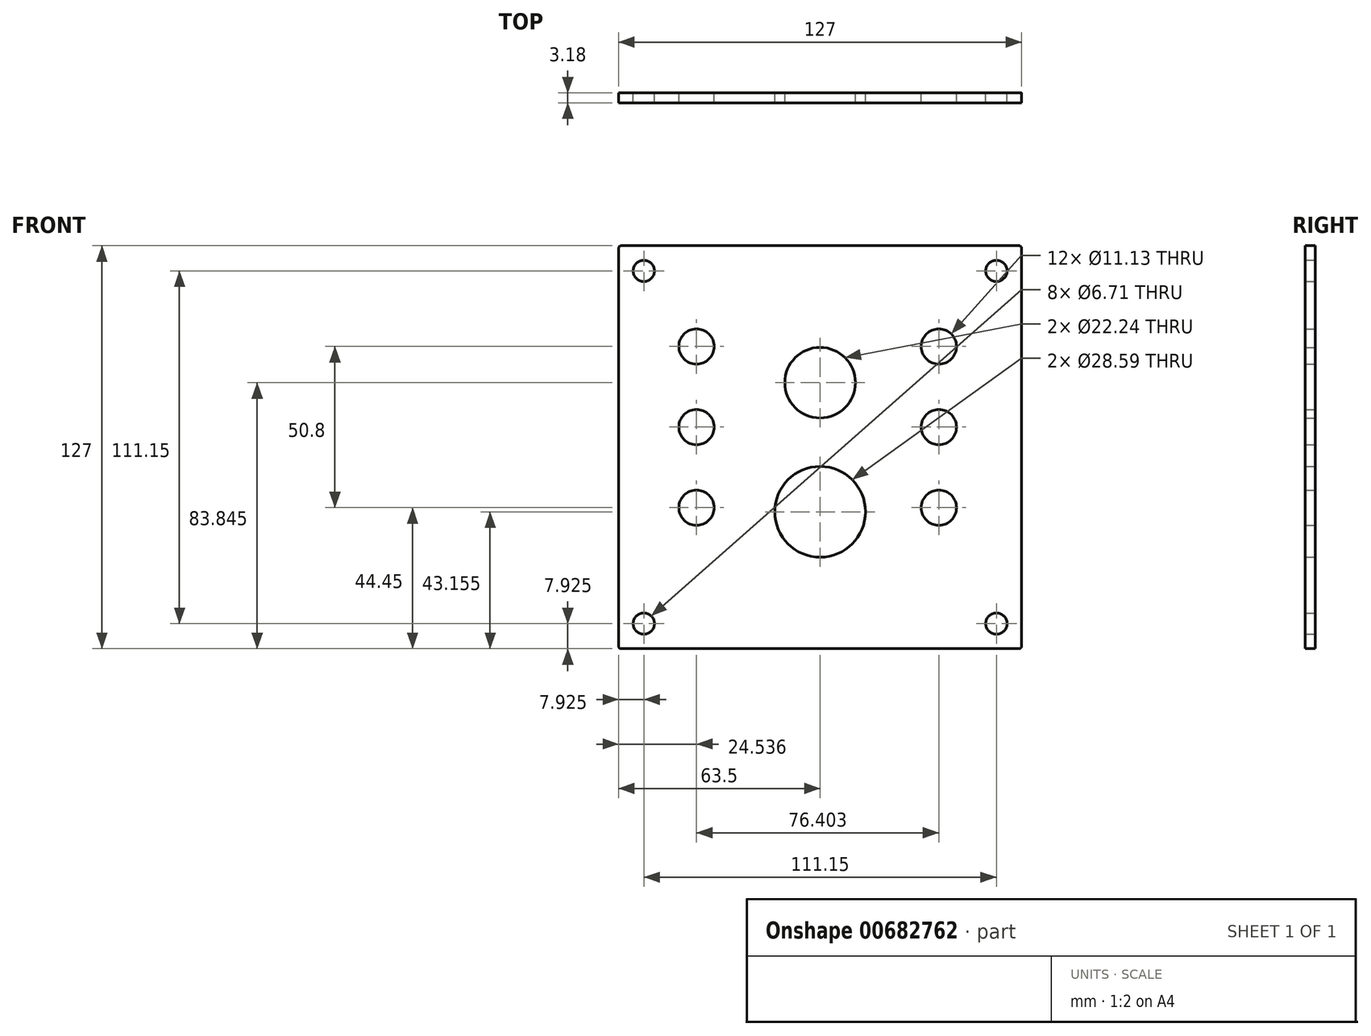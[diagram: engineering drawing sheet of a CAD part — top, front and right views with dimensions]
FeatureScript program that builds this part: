
annotation { "Feature Type Name" : "Feature", "Feature Type Description" : "" }
export const myFeature = defineFeature(function(context is Context, id is Id, definition is map)
    precondition{}
    {
        {
            var Q0;
            Q0=qCreatedBy(makeId("Front.planeOp"),FACE);
            var sketch = newSketch(context, id + "F0", { "sketchPlane" : qUnion([Q0])});
            skLineSegment(sketch, "E0.bottom", {"start": v(0.79, 0) * mm, "end": v(126.21, 0) * mm});
            skLineSegment(sketch, "E0.top", {"start": v(0.79, 127) * mm, "end": v(126.21, 127) * mm});
            skLineSegment(sketch, "E0.left", {"start": v(0, 0.79) * mm, "end": v(0, 126.21) * mm});
            skLineSegment(sketch, "E0.right", {"start": v(127, 0.79) * mm, "end": v(127, 126.21) * mm});
            skPoint(sketch, "E1.visualSharp", {"position": v(0, 127) * mm});
            skLineSegment(sketch, "E1.filletArc", {"start": v(0, 127) * mm, "end": v(0, 127) * mm});
            skPoint(sketch, "E2.visualSharp", {"position": v(0, 0) * mm});
            skLineSegment(sketch, "E2.filletArc", {"start": v(0, 0) * mm, "end": v(0, 0) * mm});
            skPoint(sketch, "E3.visualSharp", {"position": v(127, 0) * mm});
            skLineSegment(sketch, "E3.filletArc", {"start": v(127, 0) * mm, "end": v(127, 0) * mm});
            skPoint(sketch, "E4.visualSharp", {"position": v(127, 127) * mm});
            skLineSegment(sketch, "E4.filletArc", {"start": v(127, 127) * mm, "end": v(127, 127) * mm});
            skCircle(sketch, "E5", {"center": v(63.5, 83.85) * mm, "radius": 11.12 * mm});
            skCircle(sketch, "E6", {"center": v(7.92, 119.08) * mm, "radius": 3.35 * mm});
            skCircle(sketch, "E7.0.1.0", {"center": v(7.92, 7.92) * mm, "radius": 3.35 * mm});
            skCircle(sketch, "E7.1.0.0", {"center": v(119.08, 119.08) * mm, "radius": 3.35 * mm});
            skCircle(sketch, "E7.1.1.0", {"center": v(119.08, 7.92) * mm, "radius": 3.35 * mm});
            skLineSegment(sketch, "E7.direction1", {"start": v(7.92, 119.08) * mm, "end": v(119.08, 119.08) * mm, "construction": true});
            skLineSegment(sketch, "E7.direction2", {"start": v(7.92, 119.08) * mm, "end": v(7.92, 7.92) * mm, "construction": true});
            skCircle(sketch, "E8", {"center": v(63.5, 43.15) * mm, "radius": 14.3 * mm});
            skCircle(sketch, "E9", {"center": v(24.54, 95.25) * mm, "radius": 5.56 * mm});
            skCircle(sketch, "E10.0.1.0", {"center": v(24.54, 69.85) * mm, "radius": 5.56 * mm});
            skCircle(sketch, "E10.0.2.0", {"center": v(24.54, 44.45) * mm, "radius": 5.56 * mm});
            skCircle(sketch, "E10.1.0.0", {"center": v(100.94, 95.25) * mm, "radius": 5.56 * mm});
            skCircle(sketch, "E10.1.1.0", {"center": v(100.94, 69.85) * mm, "radius": 5.56 * mm});
            skCircle(sketch, "E10.1.2.0", {"center": v(100.94, 44.45) * mm, "radius": 5.56 * mm});
            skLineSegment(sketch, "E10.direction1", {"start": v(24.54, 95.25) * mm, "end": v(100.94, 95.25) * mm, "construction": true});
            skLineSegment(sketch, "E10.direction2", {"start": v(24.54, 95.25) * mm, "end": v(24.54, 69.85) * mm, "construction": true});
            skArc(sketch, "E11.filletArc", {"start": v(0.79, 127) * mm, "mid": v(0.23, 126.77) * mm, "end": v(0, 126.21) * mm});
            skArc(sketch, "E12.filletArc", {"start": v(127, 126.21) * mm, "mid": v(126.77, 126.77) * mm, "end": v(126.21, 127) * mm});
            skArc(sketch, "E13.filletArc", {"start": v(126.21, 0) * mm, "mid": v(126.77, 0.23) * mm, "end": v(127, 0.79) * mm});
            skArc(sketch, "E14.filletArc", {"start": v(0, 0.79) * mm, "mid": v(0.23, 0.23) * mm, "end": v(0.79, 0) * mm});
            skSolve(sketch);
        }
        {
            var Q0;
            Q0=makeQuery(id+"F0.imprint","IMPRINT",FACE,{"disambiguationData":[TD([[makeQuery(id+"F0.imprint","IMPRINT",EDGE,{"derivedFrom":sQuery(id+"F0.wireOp",EDGE,"E0.bottom")}),1.0]])]});
            extrude(context, id + "F1", {"entities" : qUnion([Q0]), "depth" : 3.17 * mm, "offsetDistance" : 25.4 * mm});
        }
    });
